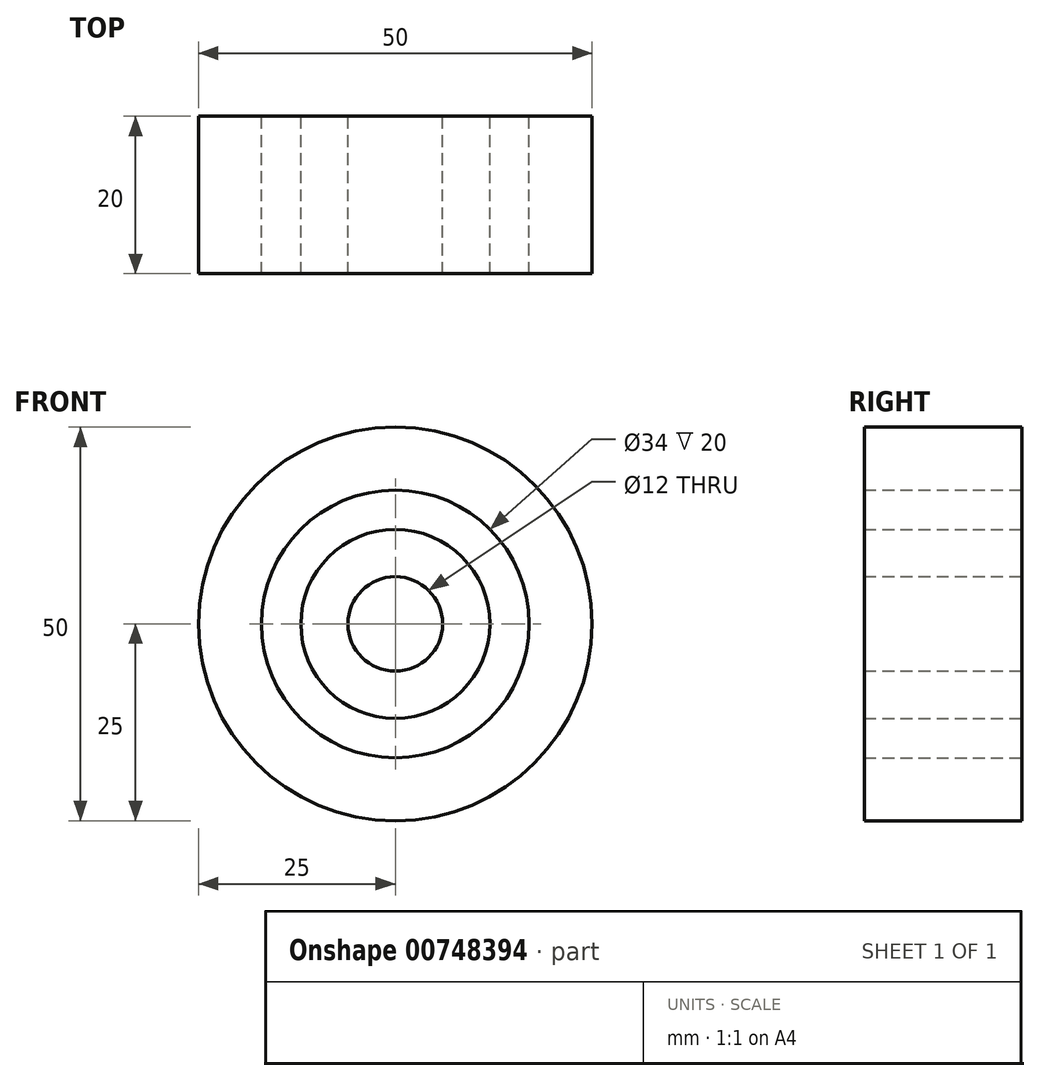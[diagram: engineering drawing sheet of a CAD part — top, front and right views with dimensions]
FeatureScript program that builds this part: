
annotation { "Feature Type Name" : "Feature", "Feature Type Description" : "" }
export const myFeature = defineFeature(function(context is Context, id is Id, definition is map)
    precondition{}
    {
        {
            var Q0;
            Q0=qCreatedBy(makeId("Top.planeOp"),FACE);
            var sketch = newSketch(context, id + "F0", { "sketchPlane" : qUnion([Q0])});
            skLineSegment(sketch, "E0.bottom", {"start": v(-25, 10) * mm, "end": v(-17, 10) * mm});
            skLineSegment(sketch, "E0.top", {"start": v(-25, -10) * mm, "end": v(-17, -10) * mm});
            skLineSegment(sketch, "E0.left", {"start": v(-25, 10) * mm, "end": v(-25, -10) * mm});
            skLineSegment(sketch, "E0.right", {"start": v(-17, 10) * mm, "end": v(-17, -10) * mm});
            skSolve(sketch);
        }
        {
            var Q0;
            Q0=qCreatedBy(makeId("Top.planeOp"),FACE);
            var sketch = newSketch(context, id + "F1", { "sketchPlane" : qUnion([Q0])});
            skLineSegment(sketch, "E1", {"start": v(0, 45.22) * mm, "end": v(0, -49.1) * mm});
            skSolve(sketch);
        }
        {
            var Q0;
            Q0=makeQuery(id+"F0.imprint","IMPRINT",FACE,{"disambiguationData":[TD([[makeQuery(id+"F0.imprint","IMPRINT",EDGE,{"derivedFrom":sQuery(id+"F0.wireOp",EDGE,"E0.bottom")}),-1.0]])]});
            var Q1;
            Q1=sQuery(id+"F1.wireOp",EDGE,"E1");
            revolve(context, id + "F2", {"surfaceOperationType" : NewSurfaceOperationType.NEW, "entities" : qUnion([Q0]), "axis" : qUnion([Q1]), "revolveType" : RevolveType.FULL});
        }
        {
            var Q0;
            Q0=qCreatedBy(makeId("Top.planeOp"),FACE);
            var sketch = newSketch(context, id + "F3", { "sketchPlane" : qUnion([Q0])});
            skLineSegment(sketch, "E2.bottom", {"start": v(-12, 10) * mm, "end": v(-6, 10) * mm});
            skLineSegment(sketch, "E2.top", {"start": v(-12, -10) * mm, "end": v(-6, -10) * mm});
            skLineSegment(sketch, "E2.left", {"start": v(-12, 10) * mm, "end": v(-12, -10) * mm});
            skLineSegment(sketch, "E2.right", {"start": v(-6, 10) * mm, "end": v(-6, -10) * mm});
            skSolve(sketch);
        }
        {
            var Q0;
            Q0=makeQuery(id+"F3.imprint","IMPRINT",FACE,{"disambiguationData":[TD([[makeQuery(id+"F3.imprint","IMPRINT",EDGE,{"derivedFrom":sQuery(id+"F3.wireOp",EDGE,"E2.bottom")}),-1.0]])]});
            var Q1;
            Q1=sQuery(id+"F1.wireOp",EDGE,"E1");
            revolve(context, id + "F4", {"surfaceOperationType" : NewSurfaceOperationType.NEW, "entities" : qUnion([Q0]), "axis" : qUnion([Q1]), "revolveType" : RevolveType.FULL});
        }
    });
